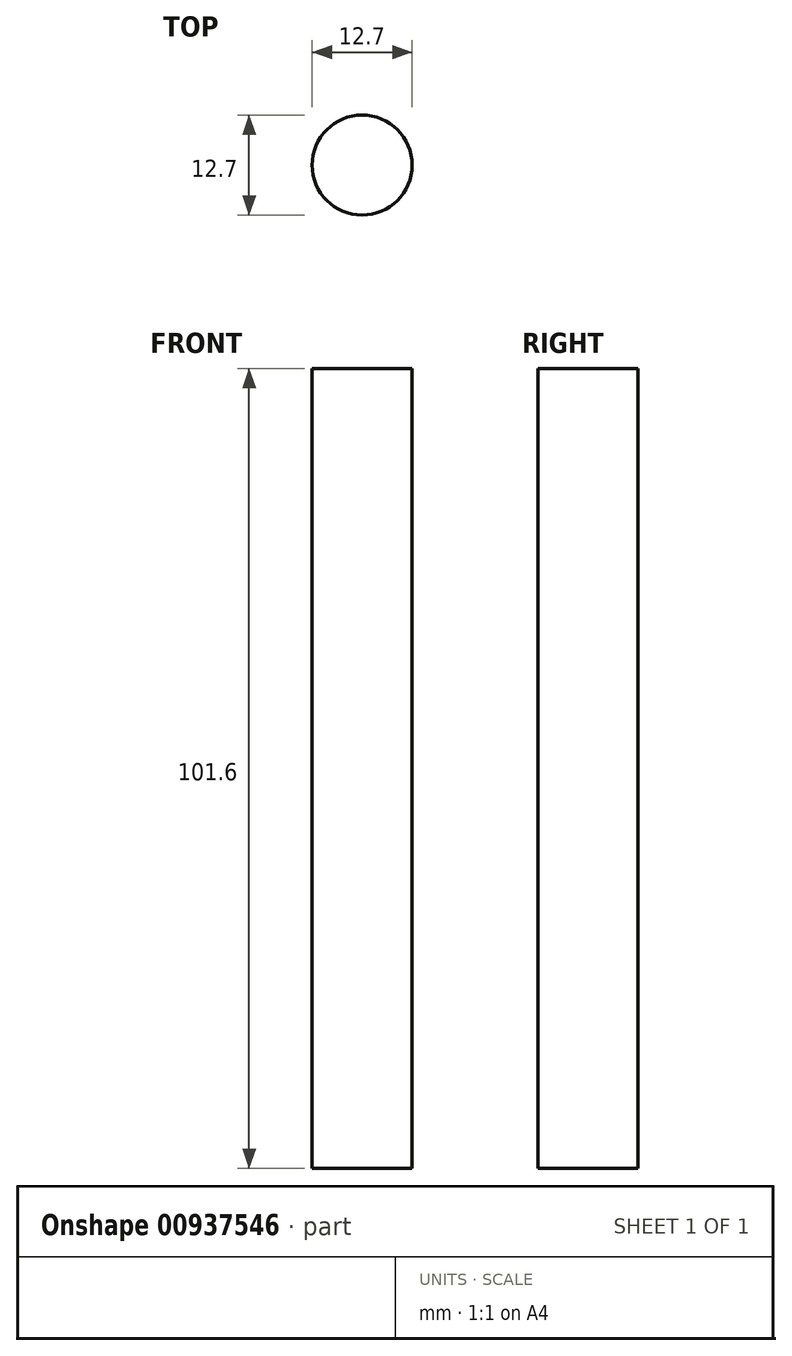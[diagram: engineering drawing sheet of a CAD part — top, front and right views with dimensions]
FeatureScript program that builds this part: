
annotation { "Feature Type Name" : "Feature", "Feature Type Description" : "" }
export const myFeature = defineFeature(function(context is Context, id is Id, definition is map)
    precondition{}
    {
        {
            var Q0;
            Q0=qCreatedBy(makeId("Top.planeOp"),FACE);
            var sketch = newSketch(context, id + "F0", { "sketchPlane" : qUnion([Q0])});
            skCircle(sketch, "E0", {"center": v(0, 0) * mm, "radius": 6.35 * mm});
            skSolve(sketch);
        }
        {
            var Q0;
            Q0 = qSketchRegion(id + "F0", true);
            extrude(context, id + "F1", {"entities" : qUnion([Q0]), "depth" : 101.6 * mm, "offsetDistance" : 25.4 * mm});
        }
    });
